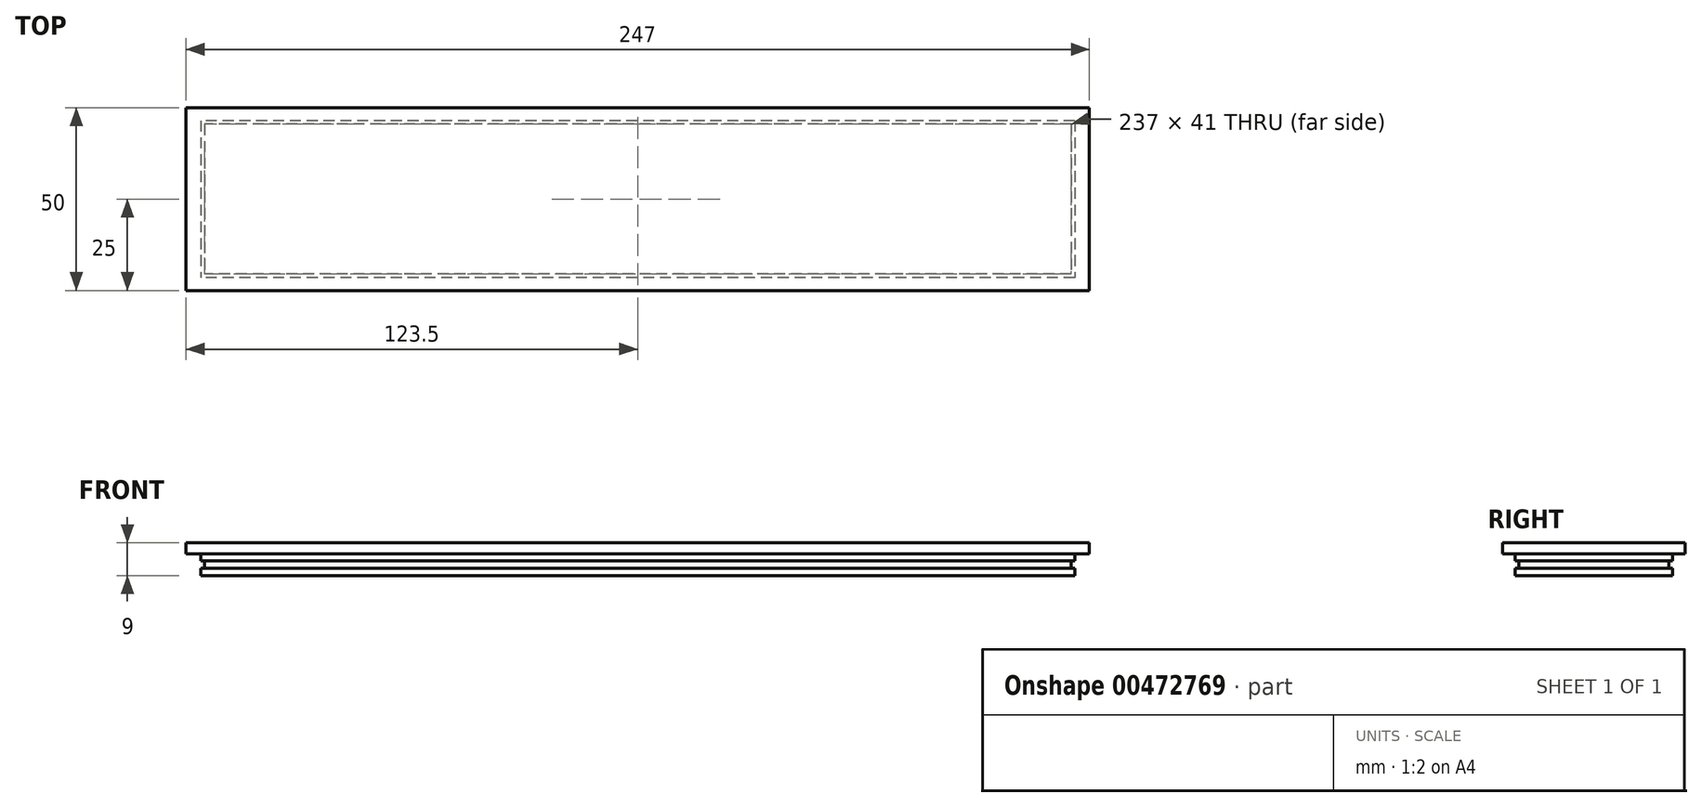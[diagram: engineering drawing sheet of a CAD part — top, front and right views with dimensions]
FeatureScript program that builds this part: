
annotation { "Feature Type Name" : "Feature", "Feature Type Description" : "" }
export const myFeature = defineFeature(function(context is Context, id is Id, definition is map)
    precondition{}
    {
        {
            var Q0;
            Q0=qCreatedBy(makeId("Top.planeOp"),FACE);
            var sketch = newSketch(context, id + "F0", { "sketchPlane" : qUnion([Q0])});
            skLineSegment(sketch, "E0.bottom", {"start": v(119.5, 21.5) * mm, "end": v(-119.5, 21.5) * mm});
            skLineSegment(sketch, "E0.top", {"start": v(119.5, -21.5) * mm, "end": v(-119.5, -21.5) * mm});
            skLineSegment(sketch, "E0.left", {"start": v(119.5, 21.5) * mm, "end": v(119.5, -21.5) * mm});
            skLineSegment(sketch, "E0.right", {"start": v(-119.5, 21.5) * mm, "end": v(-119.5, -21.5) * mm});
            skPoint(sketch, "E0.middle", {"position": v(0, 0) * mm});
            skSolve(sketch);
        }
        {
            var Q0;
            Q0=makeQuery(id+"F0.imprint","IMPRINT",FACE,{"disambiguationData":[TD([[makeQuery(id+"F0.imprint","IMPRINT",EDGE,{"derivedFrom":sQuery(id+"F0.wireOp",EDGE,"E0.bottom")}),1.0]])]});
            extrude(context, id + "F1", {"entities" : qUnion([Q0]), "depth" : 2 * mm, "offsetDistance" : 25 * mm});
        }
        {
            var Q0;
            Q0=makeQuery(id+"F1.opExtrude","CAP_FACE",FACE,{"disambiguationData":[OSD([sQuery(id+"F0.wireOp",EDGE,"E0.bottom"),sQuery(id+"F0.wireOp",EDGE,"E0.top"),sQuery(id+"F0.wireOp",EDGE,"E0.left"),sQuery(id+"F0.wireOp",EDGE,"E0.right")])],"isStart":false});
            var sketch = newSketch(context, id + "F2", { "sketchPlane" : qUnion([Q0])});
            skLineSegment(sketch, "E1.bottom", {"start": v(118.5, 20.5) * mm, "end": v(-118.5, 20.5) * mm});
            skLineSegment(sketch, "E1.top", {"start": v(118.5, -20.5) * mm, "end": v(-118.5, -20.5) * mm});
            skLineSegment(sketch, "E1.left", {"start": v(118.5, 20.5) * mm, "end": v(118.5, -20.5) * mm});
            skLineSegment(sketch, "E1.right", {"start": v(-118.5, 20.5) * mm, "end": v(-118.5, -20.5) * mm});
            skPoint(sketch, "E1.middle", {"position": v(0, 0) * mm});
            skSolve(sketch);
        }
        {
            var Q0;
            Q0=makeQuery(id+"F2.imprint","IMPRINT",FACE,{"disambiguationData":[TD([[makeQuery(id+"F2.imprint","IMPRINT",EDGE,{"derivedFrom":sQuery(id+"F2.wireOp",EDGE,"E1.bottom")}),1.0]])]});
            extrude(context, id + "F3", {"entities" : qUnion([Q0]), "operationType" : NewBodyOperationType.ADD, "depth" : 2 * mm, "offsetDistance" : 25 * mm});
        }
        {
            var Q0;
            Q0=makeQuery(id+"F3.opExtrude","CAP_FACE",FACE,{"disambiguationData":[OSD([sQuery(id+"F2.wireOp",EDGE,"E1.bottom"),sQuery(id+"F2.wireOp",EDGE,"E1.top"),sQuery(id+"F2.wireOp",EDGE,"E1.left"),sQuery(id+"F2.wireOp",EDGE,"E1.right")])],"isStart":false});
            var sketch = newSketch(context, id + "F4", { "sketchPlane" : qUnion([Q0])});
            skLineSegment(sketch, "E2.bottom", {"start": v(119.5, 21.5) * mm, "end": v(-119.5, 21.5) * mm});
            skLineSegment(sketch, "E2.top", {"start": v(119.5, -21.5) * mm, "end": v(-119.5, -21.5) * mm});
            skLineSegment(sketch, "E2.left", {"start": v(119.5, 21.5) * mm, "end": v(119.5, -21.5) * mm});
            skLineSegment(sketch, "E2.right", {"start": v(-119.5, 21.5) * mm, "end": v(-119.5, -21.5) * mm});
            skPoint(sketch, "E2.middle", {"position": v(0, 0) * mm});
            skSolve(sketch);
        }
        {
            var Q0;
            Q0 = qSketchRegion(id + "F4", true);
            extrude(context, id + "F5", {"entities" : qUnion([Q0]), "operationType" : NewBodyOperationType.ADD, "depth" : 2 * mm, "offsetDistance" : 25 * mm});
        }
        {
            var Q0;
            Q0=makeQuery(id+"F5.opExtrude","CAP_FACE",FACE,{"disambiguationData":[OSD([sQuery(id+"F4.wireOp",EDGE,"E2.bottom"),sQuery(id+"F4.wireOp",EDGE,"E2.top"),sQuery(id+"F4.wireOp",EDGE,"E2.left"),sQuery(id+"F4.wireOp",EDGE,"E2.right")])],"isStart":false});
            var sketch = newSketch(context, id + "F6", { "sketchPlane" : qUnion([Q0])});
            skLineSegment(sketch, "E3.bottom", {"start": v(123.5, 25) * mm, "end": v(-123.5, 25) * mm});
            skLineSegment(sketch, "E3.top", {"start": v(123.5, -25) * mm, "end": v(-123.5, -25) * mm});
            skLineSegment(sketch, "E3.left", {"start": v(123.5, 25) * mm, "end": v(123.5, -25) * mm});
            skLineSegment(sketch, "E3.right", {"start": v(-123.5, 25) * mm, "end": v(-123.5, -25) * mm});
            skPoint(sketch, "E3.middle", {"position": v(0, 0) * mm});
            skSolve(sketch);
        }
        {
            var Q0;
            Q0 = qSketchRegion(id + "F6", true);
            extrude(context, id + "F7", {"entities" : qUnion([Q0]), "operationType" : NewBodyOperationType.ADD, "depth" : 3 * mm, "offsetDistance" : 25 * mm});
        }
    });
